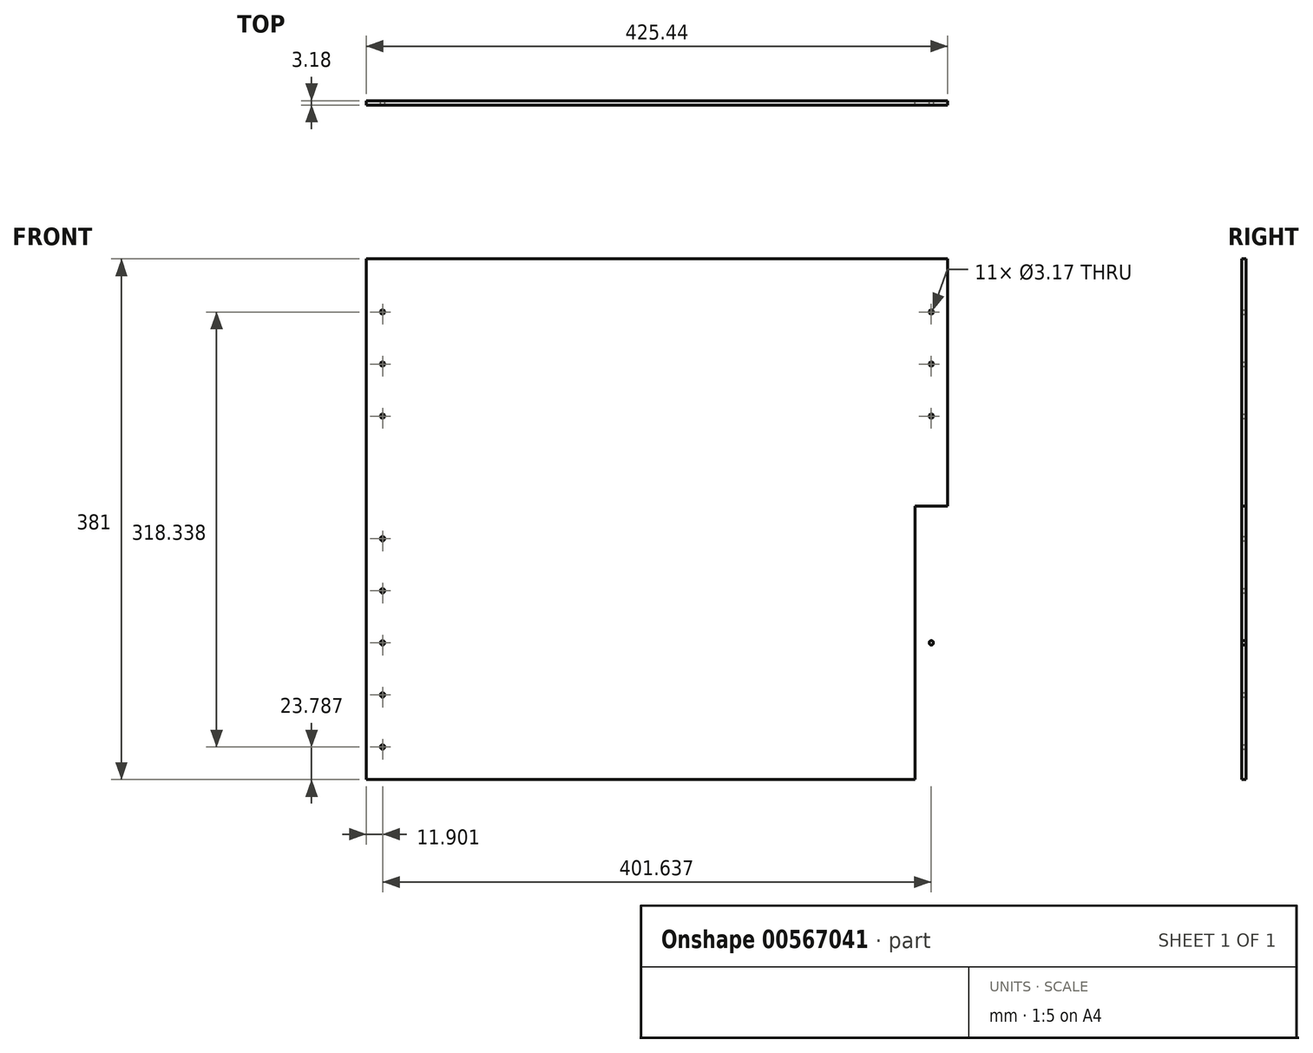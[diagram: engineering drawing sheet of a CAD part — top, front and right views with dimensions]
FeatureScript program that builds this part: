
annotation { "Feature Type Name" : "Feature", "Feature Type Description" : "" }
export const myFeature = defineFeature(function(context is Context, id is Id, definition is map)
    precondition{}
    {
        {
            var Q0;
            Q0=qCreatedBy(makeId("Front.planeOp"),FACE);
            var sketch = newSketch(context, id + "F0", { "sketchPlane" : qUnion([Q0])});
            skLineSegment(sketch, "E0.bottom", {"start": v(-212.73, 190.5) * mm, "end": v(212.73, 190.5) * mm});
            skLineSegment(sketch, "E0.top", {"start": v(-212.73, -190.5) * mm, "end": v(212.73, -190.5) * mm});
            skLineSegment(sketch, "E0.left", {"start": v(-212.73, 190.5) * mm, "end": v(-212.72, -190.5) * mm});
            skLineSegment(sketch, "E0.right", {"start": v(212.72, 190.5) * mm, "end": v(212.73, -190.5) * mm});
            skPoint(sketch, "E0.middle", {"position": v(0, 0) * mm});
            skLineSegment(sketch, "E1.bottom", {"start": v(-188.91, -190.5) * mm, "end": v(-214.31, -190.5) * mm});
            skLineSegment(sketch, "E1.top", {"start": v(-188.91, 9.47) * mm, "end": v(-214.31, 9.47) * mm});
            skLineSegment(sketch, "E1.left", {"start": v(-188.91, -190.5) * mm, "end": v(-188.91, 9.47) * mm});
            skLineSegment(sketch, "E1.right", {"start": v(-214.31, -190.5) * mm, "end": v(-214.31, 9.47) * mm});
            skLineSegment(sketch, "E2", {"start": v(-188.91, -90.51) * mm, "end": v(-212.73, -90.51) * mm, "construction": true});
            skCircle(sketch, "E3", {"center": v(-200.82, -90.51) * mm, "radius": 1.59 * mm});
            skCircle(sketch, "E4.0.1.0", {"center": v(-200.82, -52.41) * mm, "radius": 1.59 * mm});
            skCircle(sketch, "E4.0.2.0", {"center": v(-200.82, -14.31) * mm, "radius": 1.59 * mm});
            skLineSegment(sketch, "E4.direction1", {"start": v(-200.82, -90.51) * mm, "end": v(-172.24, -90.51) * mm, "construction": true});
            skLineSegment(sketch, "E4.direction2", {"start": v(-200.82, -90.51) * mm, "end": v(-200.82, -52.41) * mm, "construction": true});
            skCircle(sketch, "E5.MirrorC", {"center": v(-200.82, -128.61) * mm, "radius": 1.59 * mm});
            skCircle(sketch, "E6.MirrorC", {"center": v(-200.82, -166.71) * mm, "radius": 1.59 * mm});
            skCircle(sketch, "E7.MirrorC", {"center": v(200.82, -90.51) * mm, "radius": 1.59 * mm});
            skCircle(sketch, "E8.MirrorC", {"center": v(200.82, -52.41) * mm, "radius": 1.59 * mm});
            skLineSegment(sketch, "E9.MirrorCS", {"start": v(188.91, -90.51) * mm, "end": v(212.73, -90.51) * mm, "construction": true});
            skCircle(sketch, "E10.MirrorC", {"center": v(200.82, -14.31) * mm, "radius": 1.59 * mm});
            skCircle(sketch, "E11.MirrorC", {"center": v(200.82, -128.61) * mm, "radius": 1.59 * mm});
            skCircle(sketch, "E12.MirrorC", {"center": v(200.82, -166.71) * mm, "radius": 1.59 * mm});
            skLineSegment(sketch, "E13.MirrorCS", {"start": v(214.31, -190.5) * mm, "end": v(214.31, 9.47) * mm});
            skLineSegment(sketch, "E14.MirrorCS", {"start": v(188.91, -190.5) * mm, "end": v(214.31, -190.5) * mm});
            skLineSegment(sketch, "E15.MirrorCS", {"start": v(188.91, -190.5) * mm, "end": v(188.91, 9.47) * mm});
            skLineSegment(sketch, "E16.MirrorCS", {"start": v(188.91, 9.47) * mm, "end": v(214.31, 9.47) * mm});
            skLineSegment(sketch, "E17.MirrorCS", {"start": v(200.82, -90.51) * mm, "end": v(200.82, -52.41) * mm, "construction": true});
            skLineSegment(sketch, "E18.bottom", {"start": v(-214.31, 50.03) * mm, "end": v(-188.91, 50.03) * mm});
            skLineSegment(sketch, "E18.top", {"start": v(-214.31, 177.03) * mm, "end": v(-188.91, 177.03) * mm});
            skLineSegment(sketch, "E18.left", {"start": v(-214.31, 50.03) * mm, "end": v(-214.31, 177.03) * mm});
            skLineSegment(sketch, "E18.right", {"start": v(-188.91, 50.03) * mm, "end": v(-188.91, 177.03) * mm});
            skLineSegment(sketch, "E19", {"start": v(-188.91, 113.53) * mm, "end": v(-212.73, 113.53) * mm, "construction": true});
            skCircle(sketch, "E20", {"center": v(-200.82, 113.53) * mm, "radius": 1.59 * mm});
            skCircle(sketch, "E21.0.1.0", {"center": v(-200.82, 151.63) * mm, "radius": 1.59 * mm});
            skLineSegment(sketch, "E21.direction1", {"start": v(-200.82, 113.53) * mm, "end": v(-175.42, 113.53) * mm, "construction": true});
            skLineSegment(sketch, "E21.direction2", {"start": v(-200.82, 113.53) * mm, "end": v(-200.82, 151.63) * mm, "construction": true});
            skCircle(sketch, "E22.MirrorC", {"center": v(-200.82, 75.43) * mm, "radius": 1.59 * mm});
            skCircle(sketch, "E23.MirrorC", {"center": v(200.82, 75.43) * mm, "radius": 1.59 * mm});
            skCircle(sketch, "E24.MirrorC", {"center": v(200.82, 113.53) * mm, "radius": 1.59 * mm});
            skCircle(sketch, "E25.MirrorC", {"center": v(200.82, 151.63) * mm, "radius": 1.59 * mm});
            skLineSegment(sketch, "E26", {"start": v(-212.73, 29.13) * mm, "end": v(212.73, 29.13) * mm, "construction": true});
            skSolve(sketch);
        }
        {
            var Q0;
            {var subQ13=sQuery(id+"F0.wireOp",EDGE,"E0.bottom");Q0=makeQuery(id+"F0.imprint","IMPRINT",FACE,{"disambiguationData":[TD([[makeQuery(id+"F0.imprint","IMPRINT",EDGE,{"derivedFrom":subQ13}),-1.0]])]});}
            var Q1;
            {var subQ0=sQuery(id+"F0.wireOp",EDGE,"E18.right");Q1=makeQuery(id+"F0.imprint","IMPRINT",FACE,{"disambiguationData":[TD([[makeQuery(id+"F0.imprint","IMPRINT",EDGE,{"derivedFrom":subQ0}),1.0]])]});}
            var Q2;
            {var subQ0=sQuery(id+"F0.wireOp",EDGE,"E1.left");Q2=makeQuery(id+"F0.imprint","IMPRINT",FACE,{"disambiguationData":[TD([[makeQuery(id+"F0.imprint","IMPRINT",EDGE,{"derivedFrom":subQ0}),1.0]])]});}
            var Q3;
            Q3=makeQuery(id+"F0.imprint","IMPRINT",FACE,{"disambiguationData":[TD([[makeQuery(id+"F0.imprint","IMPRINT",EDGE,{"derivedFrom":sQuery(id+"F0.wireOp",EDGE,"E7.MirrorC")}),1.0]])]});
            extrude(context, id + "F1", {"entities" : qUnion([Q0, Q1, Q2, Q3]), "depth" : 3.17 * mm, "offsetDistance" : 25.4 * mm});
        }
    });
